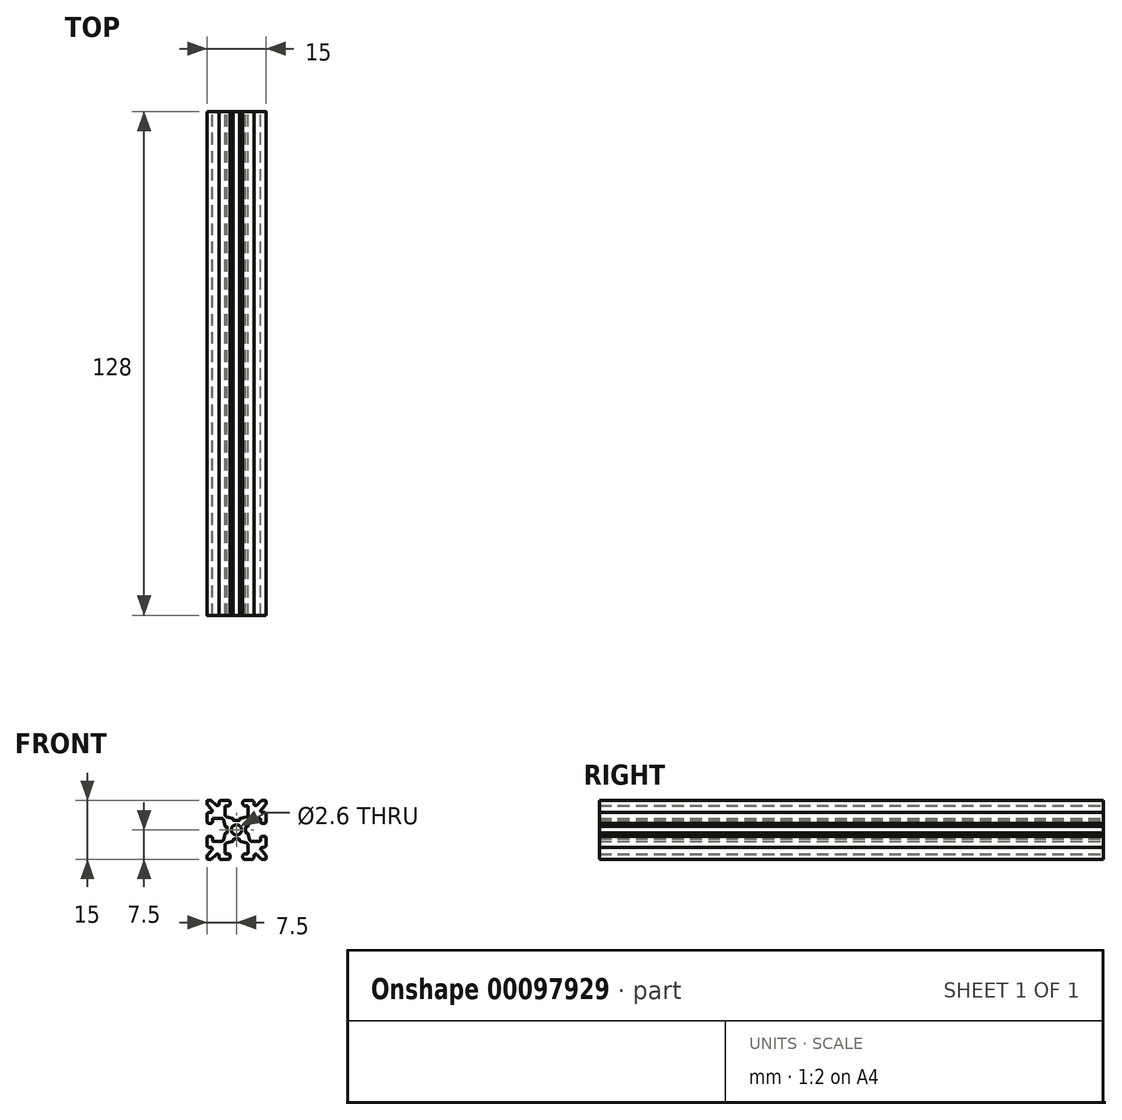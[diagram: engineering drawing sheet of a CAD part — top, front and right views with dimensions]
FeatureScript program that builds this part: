
annotation { "Feature Type Name" : "Feature", "Feature Type Description" : "" }
export const myFeature = defineFeature(function(context is Context, id is Id, definition is map)
    precondition{}
    {
        {
            var Q0;
            Q0=qCreatedBy(makeId("Front.planeOp"),FACE);
            var sketch = newSketch(context, id + "F0", { "sketchPlane" : qUnion([Q0])});
            skLineSegment(sketch, "E0.0.0", {"start": v(0.83, -2.55) * mm, "end": v(0.83, -2.77) * mm});
            skArc(sketch, "E0.0.1", {"start": v(0.83, -2.77) * mm, "mid": v(0.87, -2.9) * mm, "end": v(0.98, -2.97) * mm});
            skLineSegment(sketch, "E0.0.2", {"start": v(0.98, -2.97) * mm, "end": v(2.5, -3.31) * mm});
            skArc(sketch, "E0.0.3", {"start": v(2.5, -3.31) * mm, "mid": v(2.8, -3.49) * mm, "end": v(2.9, -3.8) * mm});
            skLineSegment(sketch, "E0.0.4", {"start": v(2.9, -3.8) * mm, "end": v(2.9, -5.9) * mm});
            skArc(sketch, "E0.0.5", {"start": v(2.9, -5.9) * mm, "mid": v(2.84, -6.04) * mm, "end": v(2.7, -6.1) * mm});
            skLineSegment(sketch, "E0.0.6", {"start": v(2.7, -6.1) * mm, "end": v(2.1, -6.1) * mm});
            skArc(sketch, "E0.0.7", {"start": v(2.1, -6.1) * mm, "mid": v(1.75, -6.25) * mm, "end": v(1.6, -6.6) * mm});
            skLineSegment(sketch, "E0.0.8", {"start": v(1.6, -6.6) * mm, "end": v(1.6, -7) * mm});
            skArc(sketch, "E0.0.9", {"start": v(1.6, -7) * mm, "mid": v(1.75, -7.35) * mm, "end": v(2.1, -7.5) * mm});
            skLineSegment(sketch, "E0.0.10", {"start": v(2.1, -7.5) * mm, "end": v(3.9, -7.5) * mm});
            skArc(sketch, "E0.0.11", {"start": v(3.9, -7.5) * mm, "mid": v(4.25, -7.35) * mm, "end": v(4.4, -7) * mm});
            skLineSegment(sketch, "E0.0.12", {"start": v(4.4, -7) * mm, "end": v(4.4, -6.67) * mm});
            skArc(sketch, "E0.0.13", {"start": v(4.4, -6.67) * mm, "mid": v(4.7, -6.2) * mm, "end": v(5.25, -6.31) * mm});
            skLineSegment(sketch, "E0.0.14", {"start": v(5.25, -6.31) * mm, "end": v(6.3, -7.35) * mm});
            skArc(sketch, "E0.0.15", {"start": v(6.3, -7.35) * mm, "mid": v(6.46, -7.46) * mm, "end": v(6.65, -7.5) * mm});
            skLineSegment(sketch, "E0.0.16", {"start": v(6.65, -7.5) * mm, "end": v(7.25, -7.5) * mm});
            skArc(sketch, "E0.0.17", {"start": v(7.25, -7.5) * mm, "mid": v(7.43, -7.43) * mm, "end": v(7.5, -7.25) * mm});
            skLineSegment(sketch, "E0.0.18", {"start": v(7.5, -7.25) * mm, "end": v(7.5, -6.65) * mm});
            skArc(sketch, "E0.0.19", {"start": v(7.5, -6.65) * mm, "mid": v(7.46, -6.46) * mm, "end": v(7.35, -6.3) * mm});
            skLineSegment(sketch, "E0.0.20", {"start": v(7.35, -6.3) * mm, "end": v(6.31, -5.25) * mm});
            skArc(sketch, "E0.0.21", {"start": v(6.31, -5.25) * mm, "mid": v(6.2, -4.7) * mm, "end": v(6.67, -4.4) * mm});
            skLineSegment(sketch, "E0.0.22", {"start": v(6.67, -4.4) * mm, "end": v(7, -4.4) * mm});
            skArc(sketch, "E0.0.23", {"start": v(7, -4.4) * mm, "mid": v(7.35, -4.25) * mm, "end": v(7.5, -3.9) * mm});
            skLineSegment(sketch, "E0.0.24", {"start": v(7.5, -3.9) * mm, "end": v(7.5, -2.1) * mm});
            skArc(sketch, "E0.0.25", {"start": v(7.5, -2.1) * mm, "mid": v(7.35, -1.75) * mm, "end": v(7, -1.6) * mm});
            skLineSegment(sketch, "E0.0.26", {"start": v(7, -1.6) * mm, "end": v(6.6, -1.6) * mm});
            skArc(sketch, "E0.0.27", {"start": v(6.6, -1.6) * mm, "mid": v(6.25, -1.75) * mm, "end": v(6.1, -2.1) * mm});
            skLineSegment(sketch, "E0.0.28", {"start": v(6.1, -2.1) * mm, "end": v(6.1, -2.7) * mm});
            skArc(sketch, "E0.0.29", {"start": v(6.1, -2.7) * mm, "mid": v(6.04, -2.84) * mm, "end": v(5.9, -2.9) * mm});
            skLineSegment(sketch, "E0.0.30", {"start": v(5.9, -2.9) * mm, "end": v(3.8, -2.9) * mm});
            skArc(sketch, "E0.0.31", {"start": v(3.8, -2.9) * mm, "mid": v(3.49, -2.8) * mm, "end": v(3.31, -2.5) * mm});
            skLineSegment(sketch, "E0.0.32", {"start": v(3.31, -2.5) * mm, "end": v(2.97, -0.98) * mm});
            skArc(sketch, "E0.0.33", {"start": v(2.97, -0.98) * mm, "mid": v(2.9, -0.87) * mm, "end": v(2.77, -0.83) * mm});
            skLineSegment(sketch, "E0.0.34", {"start": v(2.77, -0.83) * mm, "end": v(2.55, -0.83) * mm});
            skArc(sketch, "E0.0.35", {"start": v(2.55, -0.83) * mm, "mid": v(2.4, -0.77) * mm, "end": v(2.35, -0.63) * mm});
            skLineSegment(sketch, "E0.0.36", {"start": v(2.35, -0.63) * mm, "end": v(2.35, 0.63) * mm});
            skArc(sketch, "E0.0.37", {"start": v(2.35, 0.63) * mm, "mid": v(2.4, 0.77) * mm, "end": v(2.55, 0.83) * mm});
            skLineSegment(sketch, "E0.0.38", {"start": v(2.55, 0.83) * mm, "end": v(2.77, 0.83) * mm});
            skArc(sketch, "E0.0.39", {"start": v(2.77, 0.83) * mm, "mid": v(2.9, 0.87) * mm, "end": v(2.97, 0.98) * mm});
            skLineSegment(sketch, "E0.0.40", {"start": v(2.97, 0.98) * mm, "end": v(3.31, 2.5) * mm});
            skArc(sketch, "E0.0.41", {"start": v(3.31, 2.5) * mm, "mid": v(3.49, 2.8) * mm, "end": v(3.8, 2.9) * mm});
            skLineSegment(sketch, "E0.0.42", {"start": v(3.8, 2.9) * mm, "end": v(5.9, 2.9) * mm});
            skArc(sketch, "E0.0.43", {"start": v(5.9, 2.9) * mm, "mid": v(6.04, 2.84) * mm, "end": v(6.1, 2.7) * mm});
            skLineSegment(sketch, "E0.0.44", {"start": v(6.1, 2.7) * mm, "end": v(6.1, 2.1) * mm});
            skArc(sketch, "E0.0.45", {"start": v(6.1, 2.1) * mm, "mid": v(6.25, 1.75) * mm, "end": v(6.6, 1.6) * mm});
            skLineSegment(sketch, "E0.0.46", {"start": v(6.6, 1.6) * mm, "end": v(7, 1.6) * mm});
            skArc(sketch, "E0.0.47", {"start": v(7, 1.6) * mm, "mid": v(7.35, 1.75) * mm, "end": v(7.5, 2.1) * mm});
            skLineSegment(sketch, "E0.0.48", {"start": v(7.5, 2.1) * mm, "end": v(7.5, 3.9) * mm});
            skArc(sketch, "E0.0.49", {"start": v(7.5, 3.9) * mm, "mid": v(7.35, 4.25) * mm, "end": v(7, 4.4) * mm});
            skLineSegment(sketch, "E0.0.50", {"start": v(7, 4.4) * mm, "end": v(6.67, 4.4) * mm});
            skArc(sketch, "E0.0.51", {"start": v(6.67, 4.4) * mm, "mid": v(6.2, 4.7) * mm, "end": v(6.31, 5.25) * mm});
            skLineSegment(sketch, "E0.0.52", {"start": v(6.31, 5.25) * mm, "end": v(7.35, 6.3) * mm});
            skArc(sketch, "E0.0.53", {"start": v(7.35, 6.3) * mm, "mid": v(7.46, 6.46) * mm, "end": v(7.5, 6.65) * mm});
            skLineSegment(sketch, "E0.0.54", {"start": v(7.5, 6.65) * mm, "end": v(7.5, 7.25) * mm});
            skArc(sketch, "E0.0.55", {"start": v(7.5, 7.25) * mm, "mid": v(7.43, 7.43) * mm, "end": v(7.25, 7.5) * mm});
            skLineSegment(sketch, "E0.0.56", {"start": v(7.25, 7.5) * mm, "end": v(6.65, 7.5) * mm});
            skArc(sketch, "E0.0.57", {"start": v(6.65, 7.5) * mm, "mid": v(6.46, 7.46) * mm, "end": v(6.3, 7.35) * mm});
            skLineSegment(sketch, "E0.0.58", {"start": v(6.3, 7.35) * mm, "end": v(5.25, 6.31) * mm});
            skArc(sketch, "E0.0.59", {"start": v(5.25, 6.31) * mm, "mid": v(4.7, 6.2) * mm, "end": v(4.4, 6.67) * mm});
            skLineSegment(sketch, "E0.0.60", {"start": v(4.4, 6.67) * mm, "end": v(4.4, 7) * mm});
            skArc(sketch, "E0.0.61", {"start": v(4.4, 7) * mm, "mid": v(4.25, 7.35) * mm, "end": v(3.9, 7.5) * mm});
            skLineSegment(sketch, "E0.0.62", {"start": v(3.9, 7.5) * mm, "end": v(2.1, 7.5) * mm});
            skArc(sketch, "E0.0.63", {"start": v(2.1, 7.5) * mm, "mid": v(1.75, 7.35) * mm, "end": v(1.6, 7) * mm});
            skLineSegment(sketch, "E0.0.64", {"start": v(1.6, 7) * mm, "end": v(1.6, 6.6) * mm});
            skArc(sketch, "E0.0.65", {"start": v(1.6, 6.6) * mm, "mid": v(1.75, 6.25) * mm, "end": v(2.1, 6.1) * mm});
            skLineSegment(sketch, "E0.0.66", {"start": v(2.1, 6.1) * mm, "end": v(2.7, 6.1) * mm});
            skArc(sketch, "E0.0.67", {"start": v(2.7, 6.1) * mm, "mid": v(2.84, 6.04) * mm, "end": v(2.9, 5.9) * mm});
            skLineSegment(sketch, "E0.0.68", {"start": v(2.9, 5.9) * mm, "end": v(2.9, 3.8) * mm});
            skArc(sketch, "E0.0.69", {"start": v(2.9, 3.8) * mm, "mid": v(2.8, 3.49) * mm, "end": v(2.5, 3.31) * mm});
            skLineSegment(sketch, "E0.0.70", {"start": v(2.5, 3.31) * mm, "end": v(0.98, 2.97) * mm});
            skArc(sketch, "E0.0.71", {"start": v(0.98, 2.97) * mm, "mid": v(0.87, 2.9) * mm, "end": v(0.83, 2.77) * mm});
            skLineSegment(sketch, "E0.0.72", {"start": v(0.83, 2.77) * mm, "end": v(0.83, 2.55) * mm});
            skArc(sketch, "E0.0.73", {"start": v(0.83, 2.55) * mm, "mid": v(0.77, 2.4) * mm, "end": v(0.63, 2.35) * mm});
            skLineSegment(sketch, "E0.0.74", {"start": v(0.63, 2.35) * mm, "end": v(-0.63, 2.35) * mm});
            skArc(sketch, "E0.0.75", {"start": v(-0.63, 2.35) * mm, "mid": v(-0.77, 2.4) * mm, "end": v(-0.83, 2.55) * mm});
            skLineSegment(sketch, "E0.0.76", {"start": v(-0.83, 2.55) * mm, "end": v(-0.83, 2.77) * mm});
            skArc(sketch, "E0.0.77", {"start": v(-0.83, 2.77) * mm, "mid": v(-0.87, 2.9) * mm, "end": v(-0.98, 2.97) * mm});
            skLineSegment(sketch, "E0.0.78", {"start": v(-0.98, 2.97) * mm, "end": v(-2.5, 3.31) * mm});
            skArc(sketch, "E0.0.79", {"start": v(-2.5, 3.31) * mm, "mid": v(-2.8, 3.49) * mm, "end": v(-2.9, 3.8) * mm});
            skLineSegment(sketch, "E0.0.80", {"start": v(-2.9, 3.8) * mm, "end": v(-2.9, 5.9) * mm});
            skArc(sketch, "E0.0.81", {"start": v(-2.9, 5.9) * mm, "mid": v(-2.84, 6.04) * mm, "end": v(-2.7, 6.1) * mm});
            skLineSegment(sketch, "E0.0.82", {"start": v(-2.7, 6.1) * mm, "end": v(-2.1, 6.1) * mm});
            skArc(sketch, "E0.0.83", {"start": v(-2.1, 6.1) * mm, "mid": v(-1.75, 6.25) * mm, "end": v(-1.6, 6.6) * mm});
            skLineSegment(sketch, "E0.0.84", {"start": v(-1.6, 6.6) * mm, "end": v(-1.6, 7) * mm});
            skArc(sketch, "E0.0.85", {"start": v(-1.6, 7) * mm, "mid": v(-1.75, 7.35) * mm, "end": v(-2.1, 7.5) * mm});
            skLineSegment(sketch, "E0.0.86", {"start": v(-2.1, 7.5) * mm, "end": v(-3.9, 7.5) * mm});
            skArc(sketch, "E0.0.87", {"start": v(-3.9, 7.5) * mm, "mid": v(-4.25, 7.35) * mm, "end": v(-4.4, 7) * mm});
            skLineSegment(sketch, "E0.0.88", {"start": v(-4.4, 7) * mm, "end": v(-4.4, 6.67) * mm});
            skArc(sketch, "E0.0.89", {"start": v(-4.4, 6.67) * mm, "mid": v(-4.7, 6.2) * mm, "end": v(-5.25, 6.31) * mm});
            skLineSegment(sketch, "E0.0.90", {"start": v(-5.25, 6.31) * mm, "end": v(-6.3, 7.35) * mm});
            skArc(sketch, "E0.0.91", {"start": v(-6.3, 7.35) * mm, "mid": v(-6.46, 7.46) * mm, "end": v(-6.65, 7.5) * mm});
            skLineSegment(sketch, "E0.0.92", {"start": v(-6.65, 7.5) * mm, "end": v(-7.25, 7.5) * mm});
            skArc(sketch, "E0.0.93", {"start": v(-7.25, 7.5) * mm, "mid": v(-7.43, 7.43) * mm, "end": v(-7.5, 7.25) * mm});
            skLineSegment(sketch, "E0.0.94", {"start": v(-7.5, 7.25) * mm, "end": v(-7.5, 6.65) * mm});
            skArc(sketch, "E0.0.95", {"start": v(-7.5, 6.65) * mm, "mid": v(-7.46, 6.46) * mm, "end": v(-7.35, 6.3) * mm});
            skLineSegment(sketch, "E0.0.96", {"start": v(-7.35, 6.3) * mm, "end": v(-6.31, 5.25) * mm});
            skArc(sketch, "E0.0.97", {"start": v(-6.31, 5.25) * mm, "mid": v(-6.2, 4.7) * mm, "end": v(-6.67, 4.4) * mm});
            skLineSegment(sketch, "E0.0.98", {"start": v(-6.67, 4.4) * mm, "end": v(-7, 4.4) * mm});
            skArc(sketch, "E0.0.99", {"start": v(-7, 4.4) * mm, "mid": v(-7.35, 4.25) * mm, "end": v(-7.5, 3.9) * mm});
            skLineSegment(sketch, "E0.0.100", {"start": v(-7.5, 3.9) * mm, "end": v(-7.5, 2.1) * mm});
            skArc(sketch, "E0.0.101", {"start": v(-7.5, 2.1) * mm, "mid": v(-7.35, 1.75) * mm, "end": v(-7, 1.6) * mm});
            skLineSegment(sketch, "E0.0.102", {"start": v(-7, 1.6) * mm, "end": v(-6.6, 1.6) * mm});
            skArc(sketch, "E0.0.103", {"start": v(-6.6, 1.6) * mm, "mid": v(-6.25, 1.75) * mm, "end": v(-6.1, 2.1) * mm});
            skLineSegment(sketch, "E0.0.104", {"start": v(-6.1, 2.1) * mm, "end": v(-6.1, 2.7) * mm});
            skArc(sketch, "E0.0.105", {"start": v(-6.1, 2.7) * mm, "mid": v(-6.04, 2.84) * mm, "end": v(-5.9, 2.9) * mm});
            skLineSegment(sketch, "E0.0.106", {"start": v(-5.9, 2.9) * mm, "end": v(-3.8, 2.9) * mm});
            skArc(sketch, "E0.0.107", {"start": v(-3.8, 2.9) * mm, "mid": v(-3.49, 2.8) * mm, "end": v(-3.31, 2.5) * mm});
            skLineSegment(sketch, "E0.0.108", {"start": v(-3.31, 2.5) * mm, "end": v(-2.97, 0.98) * mm});
            skArc(sketch, "E0.0.109", {"start": v(-2.97, 0.98) * mm, "mid": v(-2.9, 0.87) * mm, "end": v(-2.77, 0.83) * mm});
            skLineSegment(sketch, "E0.0.110", {"start": v(-2.77, 0.83) * mm, "end": v(-2.55, 0.83) * mm});
            skArc(sketch, "E0.0.111", {"start": v(-2.55, 0.83) * mm, "mid": v(-2.4, 0.77) * mm, "end": v(-2.35, 0.63) * mm});
            skLineSegment(sketch, "E0.0.112", {"start": v(-2.35, 0.63) * mm, "end": v(-2.35, -0.63) * mm});
            skArc(sketch, "E0.0.113", {"start": v(-2.35, -0.63) * mm, "mid": v(-2.4, -0.77) * mm, "end": v(-2.55, -0.83) * mm});
            skLineSegment(sketch, "E0.0.114", {"start": v(-2.55, -0.83) * mm, "end": v(-2.77, -0.83) * mm});
            skArc(sketch, "E0.0.115", {"start": v(-2.77, -0.83) * mm, "mid": v(-2.9, -0.87) * mm, "end": v(-2.97, -0.98) * mm});
            skLineSegment(sketch, "E0.0.116", {"start": v(-2.97, -0.98) * mm, "end": v(-3.31, -2.5) * mm});
            skArc(sketch, "E0.0.117", {"start": v(-3.31, -2.5) * mm, "mid": v(-3.49, -2.8) * mm, "end": v(-3.8, -2.9) * mm});
            skLineSegment(sketch, "E0.0.118", {"start": v(-3.8, -2.9) * mm, "end": v(-5.9, -2.9) * mm});
            skArc(sketch, "E0.0.119", {"start": v(-5.9, -2.9) * mm, "mid": v(-6.04, -2.84) * mm, "end": v(-6.1, -2.7) * mm});
            skLineSegment(sketch, "E0.0.120", {"start": v(-6.1, -2.7) * mm, "end": v(-6.1, -2.1) * mm});
            skArc(sketch, "E0.0.121", {"start": v(-6.1, -2.1) * mm, "mid": v(-6.25, -1.75) * mm, "end": v(-6.6, -1.6) * mm});
            skLineSegment(sketch, "E0.0.122", {"start": v(-6.6, -1.6) * mm, "end": v(-7, -1.6) * mm});
            skArc(sketch, "E0.0.123", {"start": v(-7, -1.6) * mm, "mid": v(-7.35, -1.75) * mm, "end": v(-7.5, -2.1) * mm});
            skLineSegment(sketch, "E0.0.124", {"start": v(-7.5, -2.1) * mm, "end": v(-7.5, -3.9) * mm});
            skArc(sketch, "E0.0.125", {"start": v(-7.5, -3.9) * mm, "mid": v(-7.35, -4.25) * mm, "end": v(-7, -4.4) * mm});
            skLineSegment(sketch, "E0.0.126", {"start": v(-7, -4.4) * mm, "end": v(-6.67, -4.4) * mm});
            skArc(sketch, "E0.0.127", {"start": v(-6.67, -4.4) * mm, "mid": v(-6.2, -4.7) * mm, "end": v(-6.31, -5.25) * mm});
            skLineSegment(sketch, "E0.0.128", {"start": v(-6.31, -5.25) * mm, "end": v(-7.35, -6.3) * mm});
            skArc(sketch, "E0.0.129", {"start": v(-7.35, -6.3) * mm, "mid": v(-7.46, -6.46) * mm, "end": v(-7.5, -6.65) * mm});
            skLineSegment(sketch, "E0.0.130", {"start": v(-7.5, -6.65) * mm, "end": v(-7.5, -7.25) * mm});
            skArc(sketch, "E0.0.131", {"start": v(-7.5, -7.25) * mm, "mid": v(-7.43, -7.43) * mm, "end": v(-7.25, -7.5) * mm});
            skLineSegment(sketch, "E0.0.132", {"start": v(-7.25, -7.5) * mm, "end": v(-6.65, -7.5) * mm});
            skArc(sketch, "E0.0.133", {"start": v(-6.65, -7.5) * mm, "mid": v(-6.46, -7.46) * mm, "end": v(-6.3, -7.35) * mm});
            skLineSegment(sketch, "E0.0.134", {"start": v(-6.3, -7.35) * mm, "end": v(-5.25, -6.31) * mm});
            skArc(sketch, "E0.0.135", {"start": v(-5.25, -6.31) * mm, "mid": v(-4.7, -6.2) * mm, "end": v(-4.4, -6.67) * mm});
            skLineSegment(sketch, "E0.0.136", {"start": v(-4.4, -6.67) * mm, "end": v(-4.4, -7) * mm});
            skArc(sketch, "E0.0.137", {"start": v(-4.4, -7) * mm, "mid": v(-4.25, -7.35) * mm, "end": v(-3.9, -7.5) * mm});
            skLineSegment(sketch, "E0.0.138", {"start": v(-3.9, -7.5) * mm, "end": v(-2.1, -7.5) * mm});
            skArc(sketch, "E0.0.139", {"start": v(-2.1, -7.5) * mm, "mid": v(-1.75, -7.35) * mm, "end": v(-1.6, -7) * mm});
            skLineSegment(sketch, "E0.0.140", {"start": v(-1.6, -7) * mm, "end": v(-1.6, -6.6) * mm});
            skArc(sketch, "E0.0.141", {"start": v(-1.6, -6.6) * mm, "mid": v(-1.75, -6.25) * mm, "end": v(-2.1, -6.1) * mm});
            skLineSegment(sketch, "E0.0.142", {"start": v(-2.1, -6.1) * mm, "end": v(-2.7, -6.1) * mm});
            skArc(sketch, "E0.0.143", {"start": v(-2.7, -6.1) * mm, "mid": v(-2.84, -6.04) * mm, "end": v(-2.9, -5.9) * mm});
            skLineSegment(sketch, "E0.0.144", {"start": v(-2.9, -5.9) * mm, "end": v(-2.9, -3.8) * mm});
            skArc(sketch, "E0.0.145", {"start": v(-2.9, -3.8) * mm, "mid": v(-2.8, -3.49) * mm, "end": v(-2.5, -3.31) * mm});
            skLineSegment(sketch, "E0.0.146", {"start": v(-2.5, -3.31) * mm, "end": v(-0.98, -2.97) * mm});
            skArc(sketch, "E0.0.147", {"start": v(-0.98, -2.97) * mm, "mid": v(-0.87, -2.9) * mm, "end": v(-0.83, -2.77) * mm});
            skLineSegment(sketch, "E0.0.148", {"start": v(-0.83, -2.77) * mm, "end": v(-0.83, -2.55) * mm});
            skArc(sketch, "E0.0.149", {"start": v(-0.83, -2.55) * mm, "mid": v(-0.77, -2.4) * mm, "end": v(-0.63, -2.35) * mm});
            skLineSegment(sketch, "E0.0.150", {"start": v(-0.63, -2.35) * mm, "end": v(0.63, -2.35) * mm});
            skArc(sketch, "E0.0.151", {"start": v(0.63, -2.35) * mm, "mid": v(0.77, -2.4) * mm, "end": v(0.83, -2.55) * mm});
            skPoint(sketch, "E1", {"position": v(0, 0) * mm});
            skPoint(sketch, "E1.positionSnap0", {"position": v(0, 2.35) * mm});
            skPoint(sketch, "E1.positionSnap1", {"position": v(2.35, 0) * mm});
            skCircle(sketch, "E2", {"center": v(0, 0) * mm, "radius": 1.3 * mm});
            skSolve(sketch);
        }
        {
            var Q0;
            Q0=makeQuery(id+"F0.imprint","IMPRINT",FACE,{"disambiguationData":[TD([[makeQuery(id+"F0.imprint","IMPRINT",EDGE,{"derivedFrom":sQuery(id+"F0.wireOp",EDGE,"E0.0.0")}),1.0]])]});
            extrude(context, id + "F1", {"entities" : qUnion([Q0]), "endBound" : BoundingType.SYMMETRIC, "depth" : 128 * mm});
        }
    });
